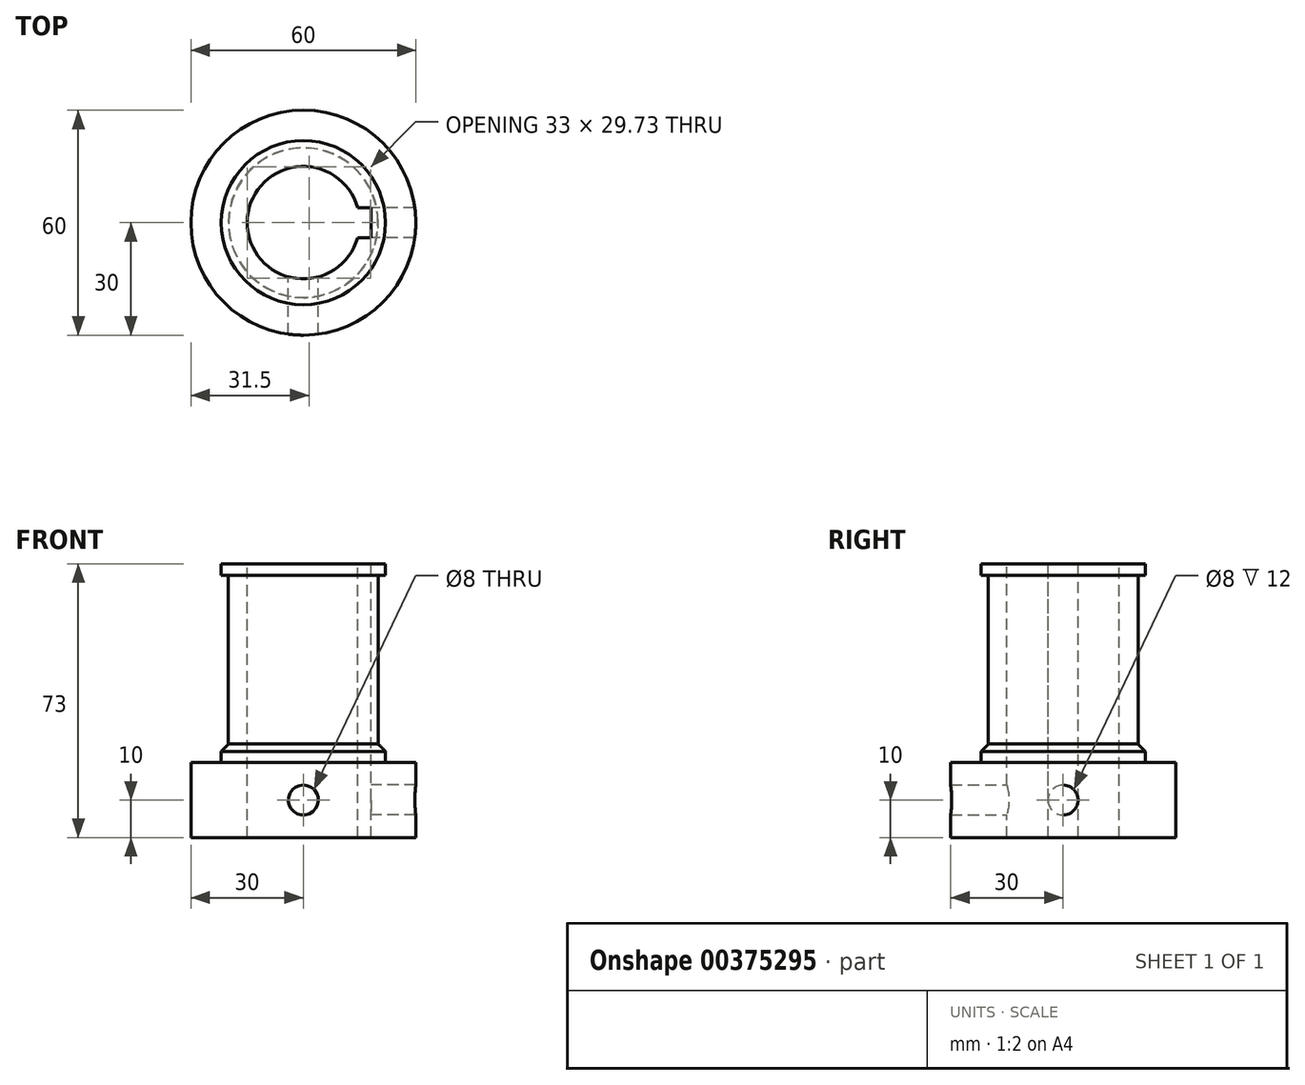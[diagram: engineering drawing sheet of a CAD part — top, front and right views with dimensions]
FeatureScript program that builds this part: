
annotation { "Feature Type Name" : "Feature", "Feature Type Description" : "" }
export const myFeature = defineFeature(function(context is Context, id is Id, definition is map)
    precondition{}
    {
        {
            var Q0;
            Q0=qCreatedBy(makeId("Top.planeOp"),FACE);
            var sketch = newSketch(context, id + "F0", { "sketchPlane" : qUnion([Q0])});
            skCircle(sketch, "E0", {"center": v(0, 0) * mm, "radius": 30 * mm});
            skSolve(sketch);
        }
        {
            var Q0;
            Q0 = qSketchRegion(id + "F0", true);
            extrude(context, id + "F1", {"entities" : qUnion([Q0]), "depth" : 20 * mm});
        }
        {
            var Q0;
            Q0=makeQuery(id+"F1.opExtrude","CAP_FACE",FACE,{"disambiguationData":[OSD([sQuery(id+"F0.wireOp",EDGE,"E0")])],"isStart":false});
            var sketch = newSketch(context, id + "F2", { "sketchPlane" : qUnion([Q0])});
            skCircle(sketch, "E1", {"center": v(0, 0) * mm, "radius": 21.9 * mm});
            skSolve(sketch);
        }
        {
            var Q0;
            Q0 = qSketchRegion(id + "F2", true);
            extrude(context, id + "F3", {"entities" : qUnion([Q0]), "operationType" : NewBodyOperationType.ADD, "depth" : 3 * mm});
        }
        {
            var Q0;
            Q0=makeQuery(id+"F3.opExtrude","CAP_FACE",FACE,{"disambiguationData":[OSD([sQuery(id+"F2.wireOp",EDGE,"E1")])],"isStart":false});
            var sketch = newSketch(context, id + "F4", { "sketchPlane" : qUnion([Q0])});
            skCircle(sketch, "E2", {"center": v(0, 0) * mm, "radius": 21.9 * mm});
            skSolve(sketch);
        }
        {
            var Q0;
            Q0 = qSketchRegion(id + "F4", true);
            extrude(context, id + "F5", {"entities" : qUnion([Q0]), "operationType" : NewBodyOperationType.ADD, "depth" : 2 * mm});
        }
        {
            var Q0;
            Q0=makeQuery(id+"F5.opExtrude","CAP_EDGE",EDGE,{"disambiguationData":[OSD([sQuery(id+"F4.wireOp",EDGE,"E2")])],"isStart":false});
            chamfer(context, id + "F6", {"entities" : qUnion([Q0]), "width" : 2 * mm, "tangentPropagation" : true});
        }
        {
            var Q0;
            Q0=makeQuery(id+"F5.opExtrude","CAP_FACE",FACE,{"disambiguationData":[OSD([sQuery(id+"F4.wireOp",EDGE,"E2")])],"isStart":false});
            var sketch = newSketch(context, id + "F7", { "sketchPlane" : qUnion([Q0])});
            skCircle(sketch, "E3", {"center": v(0, 0) * mm, "radius": 20 * mm});
            skSolve(sketch);
        }
        {
            var Q0;
            Q0 = qSketchRegion(id + "F7", true);
            extrude(context, id + "F8", {"entities" : qUnion([Q0]), "operationType" : NewBodyOperationType.ADD, "depth" : 45 * mm});
        }
        {
            var Q0;
            Q0=makeQuery(id+"F8.opExtrude","CAP_FACE",FACE,{"disambiguationData":[OSD([sQuery(id+"F7.wireOp",EDGE,"E3")])],"isStart":false});
            var sketch = newSketch(context, id + "F9", { "sketchPlane" : qUnion([Q0])});
            skCircle(sketch, "E4", {"center": v(0, 0) * mm, "radius": 21.9 * mm});
            skSolve(sketch);
        }
        {
            var Q0;
            Q0 = qSketchRegion(id + "F9", true);
            extrude(context, id + "F10", {"entities" : qUnion([Q0]), "operationType" : NewBodyOperationType.ADD, "depth" : 3 * mm});
        }
        {
            var Q0;
            Q0=makeQuery(id+"F10.opExtrude","CAP_FACE",FACE,{"disambiguationData":[OSD([sQuery(id+"F9.wireOp",EDGE,"E4")])],"isStart":false});
            var sketch = newSketch(context, id + "F11", { "sketchPlane" : qUnion([Q0])});
            skCircle(sketch, "E5", {"center": v(0, 0) * mm, "radius": 15 * mm});
            skLineSegment(sketch, "E6", {"start": v(-15, 0) * mm, "end": v(18, 0) * mm});
            skLineSegment(sketch, "E7", {"start": v(18, 0) * mm, "end": v(18, 4) * mm});
            skLineSegment(sketch, "E8", {"start": v(18, 0) * mm, "end": v(18, -4) * mm});
            skLineSegment(sketch, "E9", {"start": v(18, -4) * mm, "end": v(14.46, -4) * mm});
            skLineSegment(sketch, "E10", {"start": v(18, 4) * mm, "end": v(14.46, 4) * mm});
            skSolve(sketch);
        }
        {
            var Q0;
            Q0 = qSketchRegion(id + "F11", true);
            extrude(context, id + "F12", {"entities" : qUnion([Q0]), "operationType" : NewBodyOperationType.REMOVE, "oppositeDirection" : true, "depth" : 86.2 * mm});
        }
        {
            var Q0;
            Q0=qCreatedBy(makeId("Front.planeOp"),FACE);
            var sketch = newSketch(context, id + "F13", { "sketchPlane" : qUnion([Q0])});
            skLineSegment(sketch, "E11", {"start": v(0, 0) * mm, "end": v(0, 10) * mm});
            skCircle(sketch, "E12", {"center": v(0, 10) * mm, "radius": 4 * mm});
            skSolve(sketch);
        }
        {
            var Q0;
            Q0 = qSketchRegion(id + "F13", true);
            extrude(context, id + "F14", {"entities" : qUnion([Q0]), "operationType" : NewBodyOperationType.REMOVE, "depth" : 70 * mm});
        }
        {
            var Q0;
            Q0=qCreatedBy(makeId("Right.planeOp"),FACE);
            var sketch = newSketch(context, id + "F15", { "sketchPlane" : qUnion([Q0])});
            skLineSegment(sketch, "E13", {"start": v(0, 0) * mm, "end": v(0, 10) * mm});
            skCircle(sketch, "E14", {"center": v(0, 10) * mm, "radius": 4 * mm});
            skSolve(sketch);
        }
        {
            var Q0;
            Q0 = qSketchRegion(id + "F15", true);
            extrude(context, id + "F16", {"entities" : qUnion([Q0]), "operationType" : NewBodyOperationType.REMOVE, "depth" : 60.5 * mm});
        }
    });
